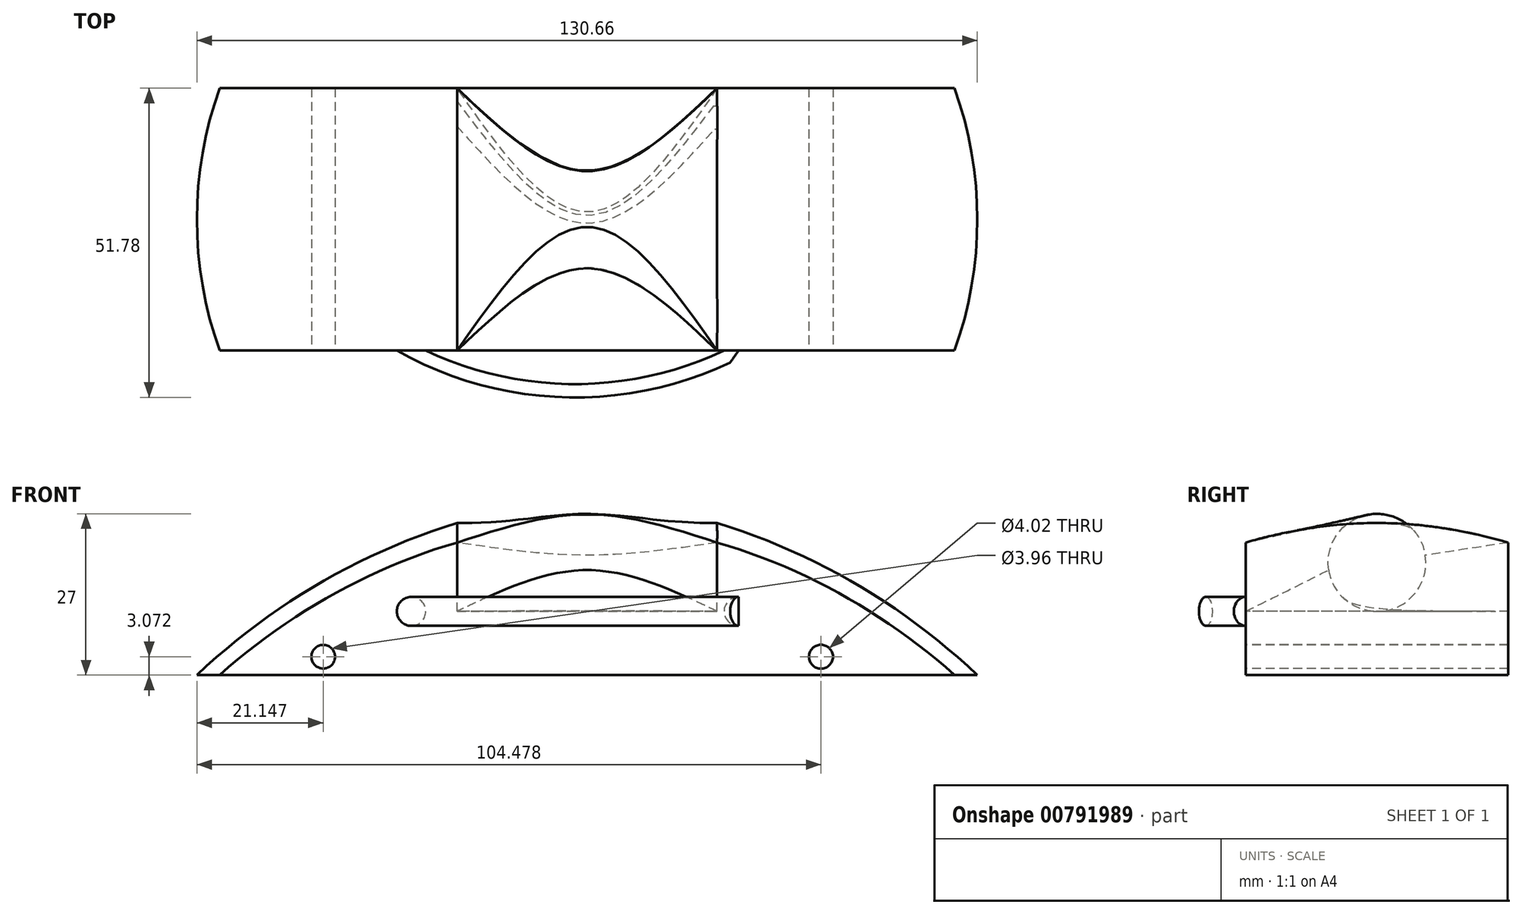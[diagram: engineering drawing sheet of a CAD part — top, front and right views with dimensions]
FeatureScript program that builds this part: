
annotation { "Feature Type Name" : "Feature", "Feature Type Description" : "" }
export const myFeature = defineFeature(function(context is Context, id is Id, definition is map)
    precondition{}
    {
        {
            var Q0;
            Q0=qCreatedBy(makeId("Front.planeOp"),FACE);
            var sketch = newSketch(context, id + "F0", { "sketchPlane" : qUnion([Q0])});
            skLineSegment(sketch, "E0", {"start": v(0, 0) * mm, "end": v(0, 29.86) * mm});
            skArc(sketch, "E1", {"start": v(0, 29.86) * mm, "mid": v(-35.15, 20.37) * mm, "end": v(-65.33, 0) * mm});
            skLineSegment(sketch, "E2", {"start": v(-65.33, 0) * mm, "end": v(0, 0) * mm});
            skSolve(sketch);
        }
        {
            var Q0;
            Q0 = qSketchRegion(id + "F0", true);
            var Q1;
            Q1=sQuery(id+"F0.wireOp",EDGE,"E0");
            revolve(context, id + "F1", {"surfaceOperationType" : NewSurfaceOperationType.NEW, "entities" : qUnion([Q0]), "axis" : qUnion([Q1]), "revolveType" : RevolveType.FULL});
        }
        {
            var Q0;
            Q0=qCreatedBy(makeId("Top.planeOp"),FACE);
            var sketch = newSketch(context, id + "F2", { "sketchPlane" : qUnion([Q0])});
            skLineSegment(sketch, "E3.bottom", {"start": v(79.71, 21.97) * mm, "end": v(-79.71, 21.97) * mm});
            skLineSegment(sketch, "E3.top", {"start": v(79.71, -21.97) * mm, "end": v(-79.71, -21.97) * mm});
            skPoint(sketch, "E3.middle", {"position": v(0, 0) * mm});
            skLineSegment(sketch, "E4", {"start": v(-79.71, 21.97) * mm, "end": v(-28.08, 73.01) * mm});
            skLineSegment(sketch, "E5", {"start": v(-28.08, 73.01) * mm, "end": v(66.7, 62.77) * mm});
            skLineSegment(sketch, "E6", {"start": v(66.7, 62.77) * mm, "end": v(79.71, 21.97) * mm});
            skLineSegment(sketch, "E7", {"start": v(-79.71, -21.97) * mm, "end": v(-49.37, -65.53) * mm});
            skLineSegment(sketch, "E8", {"start": v(-49.37, -65.53) * mm, "end": v(-3.84, -72.82) * mm});
            skLineSegment(sketch, "E9", {"start": v(-3.84, -72.82) * mm, "end": v(56.26, -65.92) * mm});
            skLineSegment(sketch, "E10", {"start": v(56.26, -65.92) * mm, "end": v(79.71, -21.97) * mm});
            skSolve(sketch);
        }
        {
            var Q0;
            Q0 = qSketchRegion(id + "F2", true);
            extrude(context, id + "F3", {"entities" : qUnion([Q0]), "operationType" : NewBodyOperationType.REMOVE, "depth" : 54.86 * mm, "offsetDistance" : 25.4 * mm});
        }
        {
            var Q0;
            Q0=makeQuery(id+"F3.boolean.opBoolean","COPY",FACE,{"derivedFrom":makeQuery(id+"F3.opExtrude","SWEPT_FACE",FACE,{"disambiguationData":[OSD([sQuery(id+"F2.wireOp",EDGE,"E3.top")])]})});
            var sketch = newSketch(context, id + "F4", { "sketchPlane" : qUnion([Q0])});
            skCircle(sketch, "E11", {"center": v(-44.18, 3.07) * mm, "radius": 1.98 * mm});
            skCircle(sketch, "E12", {"center": v(39.15, 3.07) * mm, "radius": 2 * mm});
            skLineSegment(sketch, "E13", {"start": v(-44.18, 3.07) * mm, "end": v(39.15, 3.07) * mm, "construction": true});
            skSolve(sketch);
        }
        {
            var Q0;
            Q0 = qSketchRegion(id + "F4", true);
            extrude(context, id + "F5", {"entities" : qUnion([Q0]), "operationType" : NewBodyOperationType.REMOVE, "oppositeDirection" : true, "depth" : 74.17 * mm, "offsetDistance" : 25.4 * mm});
        }
        {
            var Q0;
            Q0=qCreatedBy(makeId("Top.planeOp"),FACE);
            cPlane(context, id + "F6", {"entities" : qUnion([Q0]), "cplaneType" : CPlaneType.OFFSET, "offset" : 10.67 * mm, "width" : 152.4 * mm, "height" : 152.4 * mm});
        }
        {
            var Q0;
            Q0=qCreatedBy(id+"F6.planeOp",FACE);
            var sketch = newSketch(context, id + "F7", { "sketchPlane" : qUnion([Q0])});
            skLineSegment(sketch, "E14.bottom", {"start": v(21.78, 28.08) * mm, "end": v(-21.78, 28.08) * mm});
            skLineSegment(sketch, "E14.top", {"start": v(21.78, -28.08) * mm, "end": v(-21.78, -28.08) * mm});
            skLineSegment(sketch, "E14.left", {"start": v(21.78, 28.08) * mm, "end": v(21.78, -28.08) * mm});
            skLineSegment(sketch, "E14.right", {"start": v(-21.78, 28.08) * mm, "end": v(-21.78, -28.08) * mm});
            skPoint(sketch, "E14.middle", {"position": v(0, 0) * mm});
            skSolve(sketch);
        }
        {
            var Q0;
            Q0 = qSketchRegion(id + "F7", true);
            extrude(context, id + "F8", {"entities" : qUnion([Q0]), "operationType" : NewBodyOperationType.REMOVE, "depth" : 64.52 * mm, "offsetDistance" : 25.4 * mm});
        }
        {
            var Q0;
            Q0=makeQuery(id+"F3.boolean.opBoolean","COPY",FACE,{"derivedFrom":makeQuery(id+"F3.opExtrude","SWEPT_FACE",FACE,{"disambiguationData":[OSD([sQuery(id+"F2.wireOp",EDGE,"E3.top")])]})});
            var sketch = newSketch(context, id + "F9", { "sketchPlane" : qUnion([Q0])});
            skCircle(sketch, "E15", {"center": v(-29.44, 10.67) * mm, "radius": 2.42 * mm});
            skLineSegment(sketch, "E16", {"start": v(-29.44, 10.67) * mm, "end": v(-21.78, 10.67) * mm, "construction": true});
            skSolve(sketch);
        }
        {
            var Q0;
            Q0=qCreatedBy(id+"F6.planeOp",FACE);
            var sketch = newSketch(context, id + "F10", { "sketchPlane" : qUnion([Q0])});
            skArc(sketch, "E17", {"start": v(-29.44, -21.97) * mm, "mid": v(-2.04, -28.65) * mm, "end": v(25.35, -21.97) * mm});
            skLineSegment(sketch, "E18", {"start": v(-29.44, -21.97) * mm, "end": v(25.35, -21.97) * mm, "construction": true});
            skSolve(sketch);
        }
        {
            var Q0;
            Q0=makeQuery(id+"F9.imprint","IMPRINT",FACE,{"disambiguationData":[TD([[makeQuery(id+"F9.imprint","IMPRINT",EDGE,{"derivedFrom":sQuery(id+"F9.wireOp",EDGE,"E15")}),1.0]])]});
            var Q1;
            Q1=sQuery(id+"F10.wireOp",EDGE,"E17");
            sweep(context, id + "F11", {"operationType" : NewBodyOperationType.ADD, "profiles" : qUnion([Q0]), "path" : qUnion([Q1])});
        }
        {
            var Q0;
            Q0=qCreatedBy(makeId("Right.planeOp"),FACE);
            var sketch = newSketch(context, id + "F12", { "sketchPlane" : qUnion([Q0])});
            skCircle(sketch, "E19", {"center": v(0, 18.82) * mm, "radius": 8.18 * mm});
            skSolve(sketch);
        }
        {
            var Q1;
            Q1=makeQuery(id+"F8.boolean.opBoolean","COPY",FACE,{"derivedFrom":makeQuery(id+"F8.opExtrude","SWEPT_FACE",FACE,{"disambiguationData":[OSD([sQuery(id+"F7.wireOp",EDGE,"E14.left")])]})});
            var Q2;
            Q2=makeQuery(id+"F12.imprint","IMPRINT",FACE,{"disambiguationData":[TD([[makeQuery(id+"F12.imprint","IMPRINT",EDGE,{"derivedFrom":sQuery(id+"F12.wireOp",EDGE,"E19")}),1.0]])]});
            var Q3;
            Q3=makeQuery(id+"F8.boolean.opBoolean","COPY",FACE,{"derivedFrom":makeQuery(id+"F8.opExtrude","SWEPT_FACE",FACE,{"disambiguationData":[OSD([sQuery(id+"F7.wireOp",EDGE,"E14.right")])]})});
            loft(context, id + "F13", {"operationType" : NewBodyOperationType.ADD, "sheetProfilesArray" : [{ "sheetProfileEntities" : qUnion([Q1]) }, { "sheetProfileEntities" : qUnion([Q2]) }, { "sheetProfileEntities" : qUnion([Q3]) }]});
        }
    });
